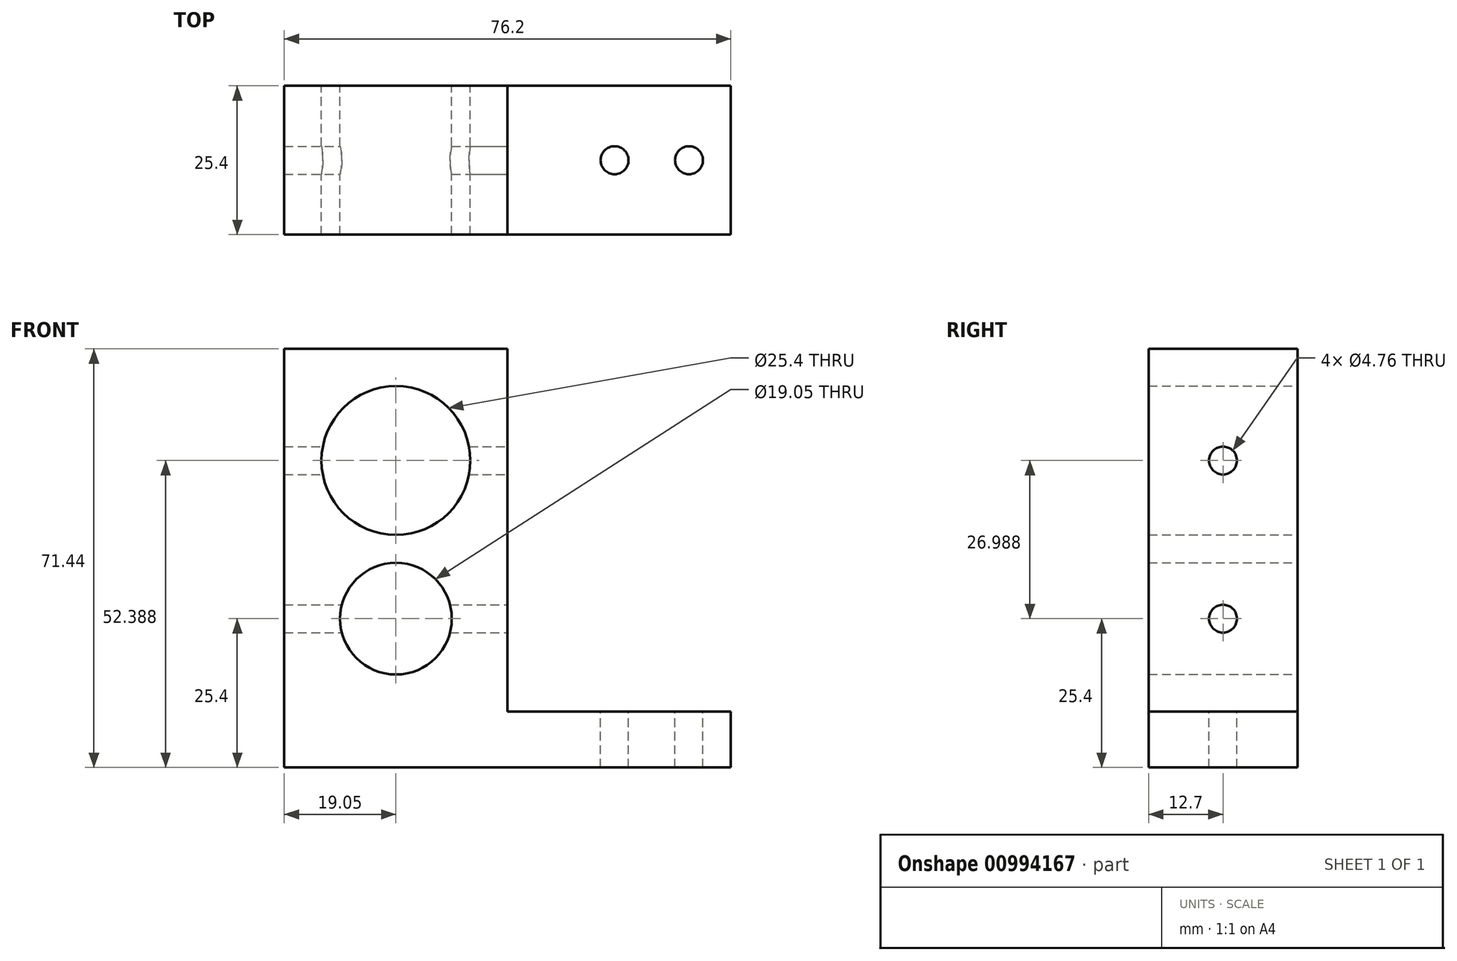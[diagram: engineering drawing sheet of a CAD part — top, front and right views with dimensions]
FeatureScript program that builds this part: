
annotation { "Feature Type Name" : "Feature", "Feature Type Description" : "" }
export const myFeature = defineFeature(function(context is Context, id is Id, definition is map)
    precondition{}
    {
        {
            var Q0;
            Q0=qCreatedBy(makeId("Front.planeOp"),FACE);
            var sketch = newSketch(context, id + "F0", { "sketchPlane" : qUnion([Q0])});
            skLineSegment(sketch, "E0.bottom", {"start": v(0, 0) * mm, "end": v(-76.2, 0) * mm});
            skLineSegment(sketch, "E0.top", {"start": v(-38.1, 71.44) * mm, "end": v(-76.2, 71.44) * mm});
            skLineSegment(sketch, "E0.left", {"start": v(0, 0) * mm, "end": v(0, 9.53) * mm});
            skLineSegment(sketch, "E0.right", {"start": v(-76.2, 0) * mm, "end": v(-76.2, 71.44) * mm});
            skCircle(sketch, "E1", {"center": v(-57.15, 52.39) * mm, "radius": 12.7 * mm});
            skCircle(sketch, "E2", {"center": v(-57.15, 25.4) * mm, "radius": 9.53 * mm});
            skLineSegment(sketch, "E3", {"start": v(-38.1, 71.44) * mm, "end": v(-38.1, 9.52) * mm});
            skLineSegment(sketch, "E4", {"start": v(-38.1, 9.52) * mm, "end": v(0, 9.53) * mm});
            skPoint(sketch, "E5.orphan", {"position": v(0, 71.44) * mm});
            skSolve(sketch);
        }
        {
            var Q0;
            Q0 = qSketchRegion(id + "F0", true);
            extrude(context, id + "F1", {"entities" : qUnion([Q0]), "depth" : 25.4 * mm, "offsetDistance" : 25.4 * mm});
        }
        {
            var Q0;
            Q0=makeQuery(id+"F1.opExtrude","SWEPT_FACE",FACE,{"disambiguationData":[OSD([sQuery(id+"F0.wireOp",EDGE,"E4")])]});
            var sketch = newSketch(context, id + "F2", { "sketchPlane" : qUnion([Q0])});
            skCircle(sketch, "E6", {"center": v(-7.14, -12.7) * mm, "radius": 2.38 * mm});
            skPoint(sketch, "E6.centerSnap0", {"position": v(0, -12.7) * mm});
            skCircle(sketch, "E7", {"center": v(-19.84, -12.7) * mm, "radius": 2.38 * mm});
            skSolve(sketch);
        }
        {
            var Q0;
            Q0 = qSketchRegion(id + "F2", true);
            extrude(context, id + "F3", {"entities" : qUnion([Q0]), "operationType" : NewBodyOperationType.REMOVE, "endBound" : BoundingType.THROUGH_ALL, "oppositeDirection" : true, "depth" : 25.4 * mm, "offsetDistance" : 25.4 * mm});
        }
        {
            var Q0;
            Q0=makeQuery(id+"F1.opExtrude","SWEPT_FACE",FACE,{"disambiguationData":[OSD([sQuery(id+"F0.wireOp",EDGE,"E3")])]});
            var sketch = newSketch(context, id + "F4", { "sketchPlane" : qUnion([Q0])});
            skCircle(sketch, "E8", {"center": v(-12.7, 25.4) * mm, "radius": 2.38 * mm});
            skCircle(sketch, "E9", {"center": v(-12.7, 52.39) * mm, "radius": 2.38 * mm});
            skSolve(sketch);
        }
        {
            var Q0;
            Q0 = qSketchRegion(id + "F4", true);
            extrude(context, id + "F5", {"entities" : qUnion([Q0]), "operationType" : NewBodyOperationType.REMOVE, "endBound" : BoundingType.THROUGH_ALL, "oppositeDirection" : true, "depth" : 25.4 * mm, "offsetDistance" : 25.4 * mm});
        }
    });
